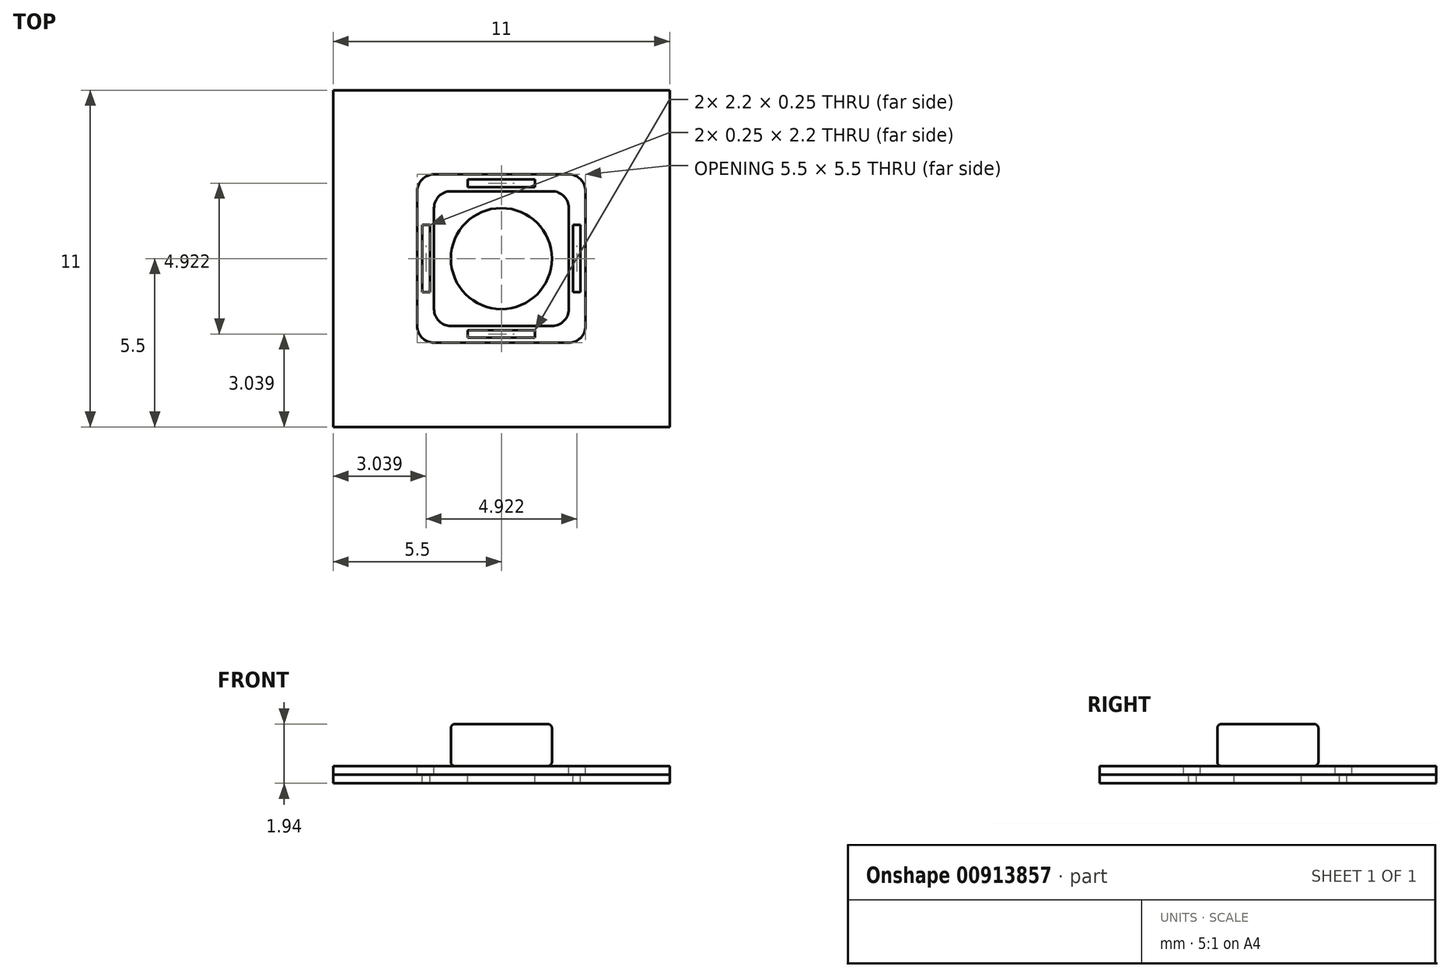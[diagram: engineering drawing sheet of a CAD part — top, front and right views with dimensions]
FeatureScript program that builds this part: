
annotation { "Feature Type Name" : "Feature", "Feature Type Description" : "" }
export const myFeature = defineFeature(function(context is Context, id is Id, definition is map)
    precondition{}
    {
        {
            var Q0;
            Q0=qCreatedBy(makeId("Top.planeOp"),FACE);
            var sketch = newSketch(context, id + "F0", { "sketchPlane" : qUnion([Q0])});
            skLineSegment(sketch, "E0.bottom", {"start": v(0, 0) * mm, "end": v(20, 0) * mm});
            skLineSegment(sketch, "E0.top", {"start": v(0, -20) * mm, "end": v(20, -20) * mm});
            skLineSegment(sketch, "E0.left", {"start": v(0, 0) * mm, "end": v(0, -20) * mm});
            skLineSegment(sketch, "E0.right", {"start": v(20, 0) * mm, "end": v(20, -20) * mm});
            skSolve(sketch);
        }
        {
            var Q0;
            Q0=qSketchRegion(id+"F0",true);
            extrude(context, id + "F1", {"entities" : qUnion([Q0]), "depth" : 0.5 * mm, "offsetDistance" : 25 * mm});
        }
        {
            var Q0;
            Q0=qCreatedBy(makeId("Right.planeOp"),FACE);
            var sketch = newSketch(context, id + "F2", { "sketchPlane" : qUnion([Q0])});
            skLineSegment(sketch, "E1.bottom", {"start": v(0, 0.5) * mm, "end": v(-20, 0.5) * mm});
            skLineSegment(sketch, "E1.top", {"start": v(0, 1.01) * mm, "end": v(-20, 1) * mm});
            skLineSegment(sketch, "E1.left", {"start": v(0, 0.5) * mm, "end": v(0, 1.01) * mm});
            skLineSegment(sketch, "E1.right", {"start": v(-20, 0.5) * mm, "end": v(-20, 1) * mm});
            skSolve(sketch);
        }
        {
            var Q0;
            Q0 = qSketchRegion(id + "F2", true);
            extrude(context, id + "F3", {"entities" : qUnion([Q0]), "depth" : 20 * mm, "offsetDistance" : 25 * mm});
        }
        {
            var Q0;
            Q0=makeQuery(id+"F3.opExtrude","SWEPT_FACE",FACE,{"disambiguationData":[OSD([sQuery(id+"F2.wireOp",EDGE,"E1.top")])]});
            var sketch = newSketch(context, id + "F4", { "sketchPlane" : qUnion([Q0])});
            skLineSegment(sketch, "E2.bottom", {"start": v(6, -5) * mm, "end": v(14, -5) * mm});
            skLineSegment(sketch, "E2.top", {"start": v(6, -15) * mm, "end": v(14, -15) * mm});
            skLineSegment(sketch, "E2.left", {"start": v(5, -6) * mm, "end": v(5, -14) * mm});
            skLineSegment(sketch, "E2.right", {"start": v(15, -6) * mm, "end": v(15, -14) * mm});
            skLineSegment(sketch, "E3.bottom", {"start": v(7, -6) * mm, "end": v(13, -6) * mm});
            skLineSegment(sketch, "E3.top", {"start": v(7, -14) * mm, "end": v(13, -14) * mm});
            skLineSegment(sketch, "E3.left", {"start": v(6, -7) * mm, "end": v(6, -13) * mm});
            skLineSegment(sketch, "E3.right", {"start": v(14, -7) * mm, "end": v(14, -13) * mm});
            skPoint(sketch, "E4.visualSharp", {"position": v(5, -5) * mm});
            skArc(sketch, "E4.filletArc", {"start": v(6, -5) * mm, "mid": v(5.3, -5.3) * mm, "end": v(5, -6) * mm});
            skPoint(sketch, "E5.visualSharp", {"position": v(15, -5) * mm});
            skArc(sketch, "E5.filletArc", {"start": v(15, -6) * mm, "mid": v(14.7, -5.3) * mm, "end": v(14, -5) * mm});
            skPoint(sketch, "E6.visualSharp", {"position": v(5, -15) * mm});
            skArc(sketch, "E6.filletArc", {"start": v(5, -14) * mm, "mid": v(5.3, -14.7) * mm, "end": v(6, -15) * mm});
            skPoint(sketch, "E7.visualSharp", {"position": v(15, -15) * mm});
            skArc(sketch, "E7.filletArc", {"start": v(14, -15) * mm, "mid": v(14.7, -14.7) * mm, "end": v(15, -14) * mm});
            skArc(sketch, "E8.filletArc", {"start": v(7, -6) * mm, "mid": v(6.3, -6.3) * mm, "end": v(6, -7) * mm});
            skArc(sketch, "E9.filletArc", {"start": v(6, -13) * mm, "mid": v(6.3, -13.7) * mm, "end": v(7, -14) * mm});
            skArc(sketch, "E10.filletArc", {"start": v(13, -14) * mm, "mid": v(13.7, -13.7) * mm, "end": v(14, -13) * mm});
            skArc(sketch, "E11.filletArc", {"start": v(14, -7) * mm, "mid": v(13.7, -6.3) * mm, "end": v(13, -6) * mm});
            skSolve(sketch);
        }
        {
            var Q0;
            Q0 = qSketchRegion(id + "F4", true);
            extrude(context, id + "F5", {"entities" : qUnion([Q0]), "operationType" : NewBodyOperationType.REMOVE, "endBound" : BoundingType.UP_TO_NEXT, "oppositeDirection" : true, "depth" : 25 * mm, "offsetDistance" : 25 * mm});
        }
        {
            var Q0;
            Q0=makeQuery(id+"F1.opExtrude","CAP_FACE",FACE,{"disambiguationData":[OSD([sQuery(id+"F0.wireOp",EDGE,"E0.bottom"),sQuery(id+"F0.wireOp",EDGE,"E0.top"),sQuery(id+"F0.wireOp",EDGE,"E0.left"),sQuery(id+"F0.wireOp",EDGE,"E0.right")])],"isStart":false});
            var sketch = newSketch(context, id + "F6", { "sketchPlane" : qUnion([Q0])});
            skLineSegment(sketch, "E12.bottom", {"start": v(8, -5.75) * mm, "end": v(12, -5.75) * mm});
            skLineSegment(sketch, "E12.top", {"start": v(8, -5.3) * mm, "end": v(12, -5.3) * mm});
            skLineSegment(sketch, "E12.left", {"start": v(8, -5.75) * mm, "end": v(8, -5.3) * mm});
            skLineSegment(sketch, "E12.right", {"start": v(12, -5.75) * mm, "end": v(12, -5.3) * mm});
            skLineSegment(sketch, "E13", {"start": v(10, 0) * mm, "end": v(10, -20) * mm, "construction": true});
            skLineSegment(sketch, "E14", {"start": v(0, -10) * mm, "end": v(20, -10) * mm, "construction": true});
            skLineSegment(sketch, "E15.MirrorCS", {"start": v(8, -14.7) * mm, "end": v(12, -14.7) * mm});
            skLineSegment(sketch, "E16.MirrorCS", {"start": v(8, -14.25) * mm, "end": v(12, -14.25) * mm});
            skLineSegment(sketch, "E17.MirrorCS", {"start": v(12, -14.25) * mm, "end": v(12, -14.7) * mm});
            skLineSegment(sketch, "E18.MirrorCS", {"start": v(8, -14.25) * mm, "end": v(8, -14.7) * mm});
            skLineSegment(sketch, "E19", {"start": v(20, 0) * mm, "end": v(0, -20) * mm, "construction": true});
            skLineSegment(sketch, "E20.MirrorCS", {"start": v(5.75, -12) * mm, "end": v(5.75, -8) * mm});
            skLineSegment(sketch, "E21.MirrorCS", {"start": v(5.3, -12) * mm, "end": v(5.3, -8) * mm});
            skLineSegment(sketch, "E22.MirrorCS", {"start": v(5.75, -12) * mm, "end": v(5.3, -12) * mm});
            skLineSegment(sketch, "E23.MirrorCS", {"start": v(5.75, -8) * mm, "end": v(5.3, -8) * mm});
            skLineSegment(sketch, "E24.MirrorCS", {"start": v(14.25, -12) * mm, "end": v(14.25, -8) * mm});
            skLineSegment(sketch, "E25.MirrorCS", {"start": v(14.7, -12) * mm, "end": v(14.7, -8) * mm});
            skLineSegment(sketch, "E26.MirrorCS", {"start": v(14.25, -12) * mm, "end": v(14.7, -12) * mm});
            skLineSegment(sketch, "E27.MirrorCS", {"start": v(14.25, -8) * mm, "end": v(14.7, -8) * mm});
            skSolve(sketch);
        }
        {
            var Q0;
            Q0 = qSketchRegion(id + "F6", true);
            extrude(context, id + "F7", {"entities" : qUnion([Q0]), "operationType" : NewBodyOperationType.REMOVE, "endBound" : BoundingType.UP_TO_NEXT, "oppositeDirection" : true, "depth" : 25 * mm, "offsetDistance" : 25 * mm});
        }
        {
            var Q0;
            Q0=qCreatedBy(makeId("Top.planeOp"),FACE);
            cPlane(context, id + "F8", {"entities" : qUnion([Q0]), "cplaneType" : CPlaneType.OFFSET, "offset" : 1.01 * mm, "width" : 150 * mm, "height" : 150 * mm});
        }
        {
            var Q0;
            Q0=qCreatedBy(id+"F8.planeOp",FACE);
            var sketch = newSketch(context, id + "F9", { "sketchPlane" : qUnion([Q0])});
            skCircle(sketch, "E28", {"center": v(10, -10) * mm, "radius": 3 * mm});
            skSolve(sketch);
        }
        {
            var Q0;
            Q0 = qSketchRegion(id + "F9", true);
            extrude(context, id + "F10", {"entities" : qUnion([Q0]), "depth" : 2.5 * mm, "offsetDistance" : 25 * mm});
        }
        {
            var Q0;
            Q0=makeQuery(id+"F10.opExtrude","CAP_EDGE",EDGE,{"disambiguationData":[OSD([sQuery(id+"F9.wireOp",EDGE,"E28")])],"isStart":false});
            var Q1;
            Q1=makeQuery(id+"F10.opExtrude","CAP_EDGE",EDGE,{"disambiguationData":[OSD([sQuery(id+"F9.wireOp",EDGE,"E28")])],"isStart":true});
            fillet(context, id + "F11", {"entities" : qUnion([Q0, Q1]), "tangentPropagation" : true, "radius" : 0.25 * mm, "defaultsChanged" : true, "vertexSettings" : [], "allowEdgeOverflow" : false});
        }
        {
            var Q0;
            Q0=makeQuery(id+"F1.opExtrude","SWEPT_BODY",BODY,{"disambiguationData":[OSD([sQuery(id+"F0.wireOp",EDGE,"E0.bottom"),sQuery(id+"F0.wireOp",EDGE,"E0.top"),sQuery(id+"F0.wireOp",EDGE,"E0.left"),sQuery(id+"F0.wireOp",EDGE,"E0.right")])]});
            var Q1;
            Q1=makeQuery(id+"F5.boolean.opBoolean","SPLIT",BODY,{"disambiguationData":[OD(0.0)],"derivedFrom":makeQuery(id+"F3.opExtrude","SWEPT_BODY",BODY,{"disambiguationData":[OSD([sQuery(id+"F2.wireOp",EDGE,"E1.bottom"),sQuery(id+"F2.wireOp",EDGE,"E1.top"),sQuery(id+"F2.wireOp",EDGE,"E1.left"),sQuery(id+"F2.wireOp",EDGE,"E1.right")])]})});
            var Q2;
            Q2=makeQuery(id+"F5.boolean.opBoolean","SPLIT",BODY,{"disambiguationData":[OD(1.0)],"derivedFrom":makeQuery(id+"F3.opExtrude","SWEPT_BODY",BODY,{"disambiguationData":[OSD([sQuery(id+"F2.wireOp",EDGE,"E1.bottom"),sQuery(id+"F2.wireOp",EDGE,"E1.top"),sQuery(id+"F2.wireOp",EDGE,"E1.left"),sQuery(id+"F2.wireOp",EDGE,"E1.right")])]})});
            var Q3;
            Q3=makeQuery(id+"F10.opExtrude","SWEPT_BODY",BODY,{"disambiguationData":[OSD([sQuery(id+"F9.wireOp",EDGE,"E28")])]});
            var Q4;
            Q4=makeQuery(id+"F3.opExtrude","CAP_VERTEX",VERTEX,{"disambiguationData":[OSD([sQuery(id+"F2.wireOp",EDGE,"E1.top"),sQuery(id+"F2.wireOp",EDGE,"E1.left")])],"isStart":true});
            transform(context, id + "F12", {"entities" : qUnion([Q0, Q1, Q2, Q3]), "transformType" : TransformType.SCALE_UNIFORMLY, "scale" : 0.55, "scalePoint" : qUnion([Q4]), "makeCopy" : false});
        }
    });
